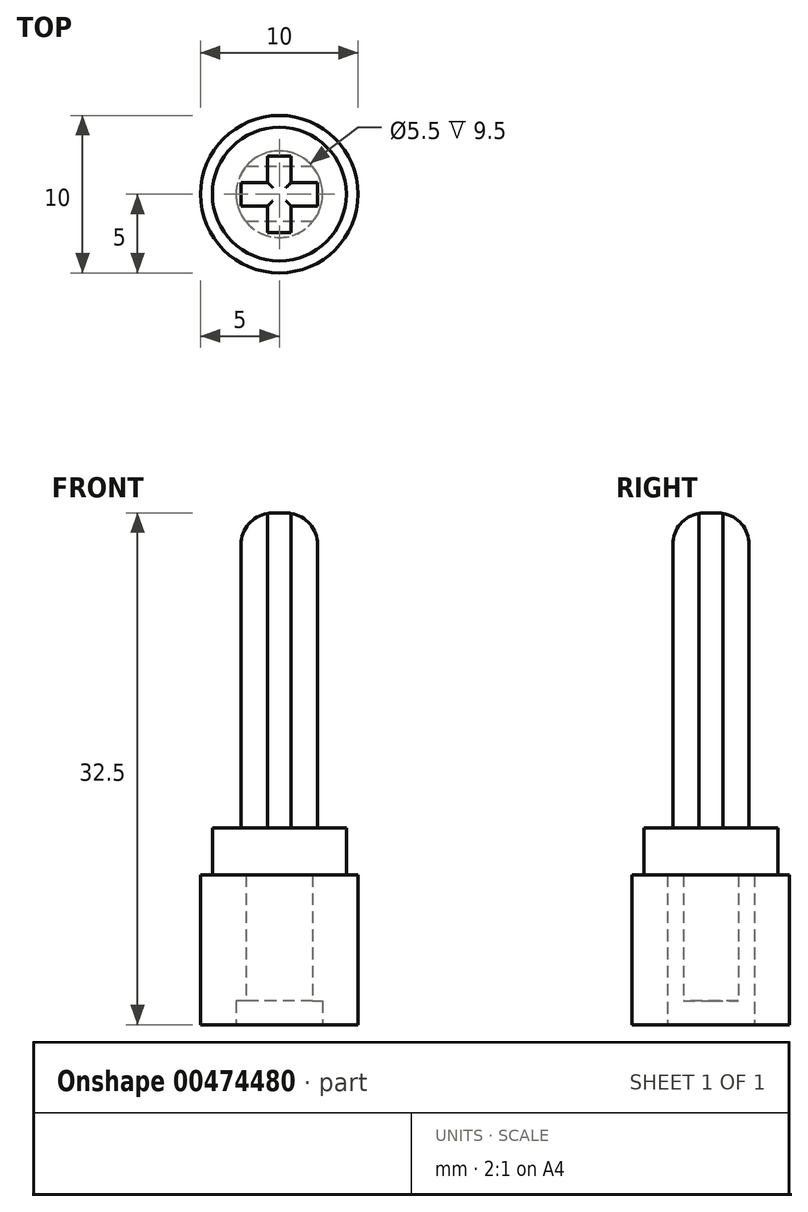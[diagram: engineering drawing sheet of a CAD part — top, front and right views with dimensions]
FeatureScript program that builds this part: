
annotation { "Feature Type Name" : "Feature", "Feature Type Description" : "" }
export const myFeature = defineFeature(function(context is Context, id is Id, definition is map)
    precondition{}
    {
        {
            var Q0;
            Q0=qCreatedBy(makeId("Top.planeOp"),FACE);
            var sketch = newSketch(context, id + "F0", { "sketchPlane" : qUnion([Q0])});
            skCircle(sketch, "E0", {"center": v(0, 0) * mm, "radius": 5 * mm});
            skCircle(sketch, "E1", {"center": v(0, 0) * mm, "radius": 2.75 * mm});
            skLineSegment(sketch, "E2.bottom", {"start": v(6.8, -1.75) * mm, "end": v(-6.8, -1.75) * mm});
            skLineSegment(sketch, "E2.top", {"start": v(6.8, 1.75) * mm, "end": v(-6.8, 1.75) * mm});
            skLineSegment(sketch, "E2.left", {"start": v(6.8, -1.75) * mm, "end": v(6.8, 1.75) * mm, "construction": true});
            skLineSegment(sketch, "E2.right", {"start": v(-6.8, -1.75) * mm, "end": v(-6.8, 1.75) * mm, "construction": true});
            skSolve(sketch);
        }
        {
            var Q0;
            {var subQ0=sQuery(id+"F0.wireOp",EDGE,"E2.top");var subQ1=sQuery(id+"F0.wireOp",EDGE,"E0");var subQ2=makeQuery(id+"F0.imprint","INTERSECT",VERTEX,{"disambiguationData":[OD(0.0)],"derivedFrom":[subQ1,subQ0]});Q0=makeQuery(id+"F0.imprint","IMPRINT",FACE,{"disambiguationData":[TD([[makeQuery(id+"F0.imprint","IMPRINT",EDGE,{"disambiguationData":[TD([[subQ2,1.0]])],"derivedFrom":subQ1}),1.0]])]});}
            var Q1;
            {var subQ0=sQuery(id+"F0.wireOp",EDGE,"E2.top");var subQ1=sQuery(id+"F0.wireOp",EDGE,"E1");var subQ2=makeQuery(id+"F0.imprint","INTERSECT",VERTEX,{"disambiguationData":[OD(0.0)],"derivedFrom":[subQ1,subQ0]});Q1=makeQuery(id+"F0.imprint","IMPRINT",FACE,{"disambiguationData":[TD([[makeQuery(id+"F0.imprint","IMPRINT",EDGE,{"disambiguationData":[TD([[subQ2,1.0]])],"derivedFrom":subQ1}),1.0]])]});}
            var Q2;
            {var subQ0=sQuery(id+"F0.wireOp",EDGE,"E2.top");var subQ1=sQuery(id+"F0.wireOp",EDGE,"E0");var subQ2=makeQuery(id+"F0.imprint","INTERSECT",VERTEX,{"disambiguationData":[OD(1.0)],"derivedFrom":[subQ1,subQ0]});Q2=makeQuery(id+"F0.imprint","IMPRINT",FACE,{"disambiguationData":[TD([[makeQuery(id+"F0.imprint","IMPRINT",EDGE,{"disambiguationData":[TD([[subQ2,1.0]])],"derivedFrom":subQ1}),1.0]])]});}
            var Q3;
            {var subQ0=sQuery(id+"F0.wireOp",EDGE,"E2.top");var subQ1=sQuery(id+"F0.wireOp",EDGE,"E0");var subQ2=makeQuery(id+"F0.imprint","INTERSECT",VERTEX,{"disambiguationData":[OD(0.0)],"derivedFrom":[subQ1,subQ0]});Q3=makeQuery(id+"F0.imprint","IMPRINT",FACE,{"disambiguationData":[TD([[makeQuery(id+"F0.imprint","IMPRINT",EDGE,{"disambiguationData":[TD([[subQ2,-1.0]])],"derivedFrom":subQ1}),1.0]])]});}
            var Q4;
            {var subQ0=sQuery(id+"F0.wireOp",EDGE,"E2.bottom");var subQ1=sQuery(id+"F0.wireOp",EDGE,"E1");var subQ2=makeQuery(id+"F0.imprint","INTERSECT",VERTEX,{"disambiguationData":[OD(0.0)],"derivedFrom":[subQ1,subQ0]});Q4=makeQuery(id+"F0.imprint","IMPRINT",FACE,{"disambiguationData":[TD([[makeQuery(id+"F0.imprint","IMPRINT",EDGE,{"disambiguationData":[TD([[subQ2,-1.0]])],"derivedFrom":subQ1}),1.0]])]});}
            var Q5;
            {var subQ0=sQuery(id+"F0.wireOp",EDGE,"E2.bottom");var subQ1=sQuery(id+"F0.wireOp",EDGE,"E0");var subQ2=makeQuery(id+"F0.imprint","INTERSECT",VERTEX,{"disambiguationData":[OD(0.0)],"derivedFrom":[subQ1,subQ0]});Q5=makeQuery(id+"F0.imprint","IMPRINT",FACE,{"disambiguationData":[TD([[makeQuery(id+"F0.imprint","IMPRINT",EDGE,{"disambiguationData":[TD([[subQ2,-1.0]])],"derivedFrom":subQ1}),1.0]])]});}
            extrude(context, id + "F1", {"entities" : qUnion([Q0, Q1, Q2, Q3, Q4, Q5]), "depth" : 8 * mm});
        }
        {
            var Q0;
            Q0=makeQuery(id+"F1.opExtrude","CAP_FACE",FACE,{"disambiguationData":[OSD([sQuery(id+"F0.wireOp",EDGE,"E0"),sQuery(id+"F0.wireOp",EDGE,"E1"),sQuery(id+"F0.wireOp",EDGE,"E2.bottom"),sQuery(id+"F0.wireOp",EDGE,"E2.top")])],"isStart":false});
            var sketch = newSketch(context, id + "F2", { "sketchPlane" : qUnion([Q0])});
            skCircle(sketch, "E3", {"center": v(0, 0) * mm, "radius": 4.25 * mm});
            skSolve(sketch);
        }
        {
            var Q0;
            Q0 = qSketchRegion(id + "F2", true);
            extrude(context, id + "F3", {"entities" : qUnion([Q0]), "operationType" : NewBodyOperationType.ADD, "depth" : 3 * mm});
        }
        {
            var Q0;
            Q0=makeQuery(id+"F3.opExtrude","CAP_FACE",FACE,{"disambiguationData":[OSD([sQuery(id+"F2.wireOp",EDGE,"E3")])],"isStart":false});
            var sketch = newSketch(context, id + "F4", { "sketchPlane" : qUnion([Q0])});
            skLineSegment(sketch, "E4.bottom", {"start": v(2.43, -0.75) * mm, "end": v(-2.42, -0.75) * mm});
            skLineSegment(sketch, "E4.top", {"start": v(2.43, 0.75) * mm, "end": v(-2.42, 0.75) * mm});
            skLineSegment(sketch, "E4.left", {"start": v(2.43, -0.75) * mm, "end": v(2.43, 0.75) * mm});
            skLineSegment(sketch, "E4.right", {"start": v(-2.42, -0.75) * mm, "end": v(-2.42, 0.75) * mm});
            skPoint(sketch, "E4.middle", {"position": v(0, 0) * mm});
            skLineSegment(sketch, "E5.bottom", {"start": v(0.75, -2.43) * mm, "end": v(-0.75, -2.43) * mm});
            skLineSegment(sketch, "E5.top", {"start": v(0.75, 2.43) * mm, "end": v(-0.75, 2.43) * mm});
            skLineSegment(sketch, "E5.left", {"start": v(0.75, -2.43) * mm, "end": v(0.75, 2.43) * mm});
            skLineSegment(sketch, "E5.right", {"start": v(-0.75, -2.43) * mm, "end": v(-0.75, 2.43) * mm});
            skSolve(sketch);
        }
        {
            var Q0;
            {var subQ0=sQuery(id+"F4.wireOp",EDGE,"E4.right");Q0=makeQuery(id+"F4.imprint","IMPRINT",FACE,{"disambiguationData":[TD([[makeQuery(id+"F4.imprint","IMPRINT",EDGE,{"derivedFrom":subQ0}),-1.0]])]});}
            var Q1;
            {var subQ0=sQuery(id+"F4.wireOp",EDGE,"E5.left");var subQ1=sQuery(id+"F4.wireOp",EDGE,"E4.bottom");var subQ2=makeQuery(id+"F4.imprint","INTERSECT",VERTEX,{"derivedFrom":[subQ1,subQ0]});Q1=makeQuery(id+"F4.imprint","IMPRINT",FACE,{"disambiguationData":[TD([[makeQuery(id+"F4.imprint","IMPRINT",EDGE,{"disambiguationData":[TD([[subQ2,-1.0]])],"derivedFrom":subQ1}),-1.0]])]});}
            var Q2;
            {var subQ5=sQuery(id+"F4.wireOp",EDGE,"E5.top");Q2=makeQuery(id+"F4.imprint","IMPRINT",FACE,{"disambiguationData":[TD([[makeQuery(id+"F4.imprint","IMPRINT",EDGE,{"derivedFrom":subQ5}),1.0]])]});}
            var Q3;
            {var subQ0=sQuery(id+"F4.wireOp",EDGE,"E4.left");Q3=makeQuery(id+"F4.imprint","IMPRINT",FACE,{"disambiguationData":[TD([[makeQuery(id+"F4.imprint","IMPRINT",EDGE,{"derivedFrom":subQ0}),1.0]])]});}
            var Q4;
            {var subQ5=sQuery(id+"F4.wireOp",EDGE,"E5.bottom");Q4=makeQuery(id+"F4.imprint","IMPRINT",FACE,{"disambiguationData":[TD([[makeQuery(id+"F4.imprint","IMPRINT",EDGE,{"derivedFrom":subQ5}),-1.0]])]});}
            extrude(context, id + "F5", {"entities" : qUnion([Q0, Q1, Q2, Q3, Q4]), "operationType" : NewBodyOperationType.ADD, "depth" : 20 * mm});
        }
        {
            var Q0;
            Q0=makeQuery(id+"F5.opExtrude","CAP_EDGE",EDGE,{"disambiguationData":[OSD([sQuery(id+"F4.wireOp",EDGE,"E5.top")])],"isStart":false});
            var Q1;
            Q1=makeQuery(id+"F5.opExtrude","CAP_EDGE",EDGE,{"disambiguationData":[OSD([sQuery(id+"F4.wireOp",EDGE,"E4.left")])],"isStart":false});
            var Q2;
            Q2=makeQuery(id+"F5.opExtrude","CAP_EDGE",EDGE,{"disambiguationData":[OSD([sQuery(id+"F4.wireOp",EDGE,"E5.bottom")])],"isStart":false});
            var Q3;
            Q3=makeQuery(id+"F5.opExtrude","CAP_EDGE",EDGE,{"disambiguationData":[OSD([sQuery(id+"F4.wireOp",EDGE,"E4.right")])],"isStart":false});
            fillet(context, id + "F6", {"entities" : qUnion([Q0, Q1, Q2, Q3]), "radius" : 2 * mm, "tangentPropagation" : true, "allowEdgeOverflow" : false});
        }
        {
            var Q0;
            Q0=makeQuery(id+"F1.opExtrude","CAP_FACE",FACE,{"disambiguationData":[OSD([sQuery(id+"F0.wireOp",EDGE,"E0"),sQuery(id+"F0.wireOp",EDGE,"E1"),sQuery(id+"F0.wireOp",EDGE,"E2.bottom"),sQuery(id+"F0.wireOp",EDGE,"E2.top")])],"isStart":true});
            var sketch = newSketch(context, id + "F7", { "sketchPlane" : qUnion([Q0])});
            skCircle(sketch, "E6", {"center": v(0, 0) * mm, "radius": 2.75 * mm});
            skCircle(sketch, "E7", {"center": v(0, 0) * mm, "radius": 5 * mm});
            skSolve(sketch);
        }
        {
            var Q0;
            Q0=makeQuery(id+"F7.imprint","IMPRINT",FACE,{"disambiguationData":[TD([[makeQuery(id+"F7.imprint","IMPRINT",EDGE,{"derivedFrom":sQuery(id+"F7.wireOp",EDGE,"E7")}),-1.0]])]});
            extrude(context, id + "F8", {"entities" : qUnion([Q0]), "operationType" : NewBodyOperationType.ADD, "depth" : 1.5 * mm});
        }
    });
